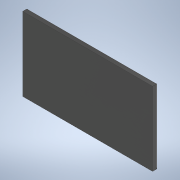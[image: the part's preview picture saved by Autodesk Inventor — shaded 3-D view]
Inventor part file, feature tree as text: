
AUTODESK INVENTOR PART (.ipt)
format: ipt  version: 2020 (Build 240168000, 168)  size: 108,032 bytes
history: native  units: in
note: dims shown in document units (in); Inventor stores cm internally (conversion verified against a paired STEP export)
features: sketch x3, extrude x2, fillet x1
ambient origin geometry x8: Origin, YZ Plane, XZ Plane, XY Plane, X Axis, Y Axis, Z Axis, Center Point
bodies: Solid1 (feature_tree)
feature tree (6):
  extrude  "Extrusion1"  Depth=37.5984in
  fillet  "Fillet1"  Radius=2.4016in
  sketch  "Sketch2"  dims[d4=0.3937in d5=0.1969in d6=0.0in]
  extrude  "Extrusion2"  Depth=0.1969in TaperAngle=0.0deg
  sketch  "Sketch1"  dims[d0=66.2992in d1=37.5984in d2=2.4016in d3=0.0in]
  sketch  "Sketch3"
